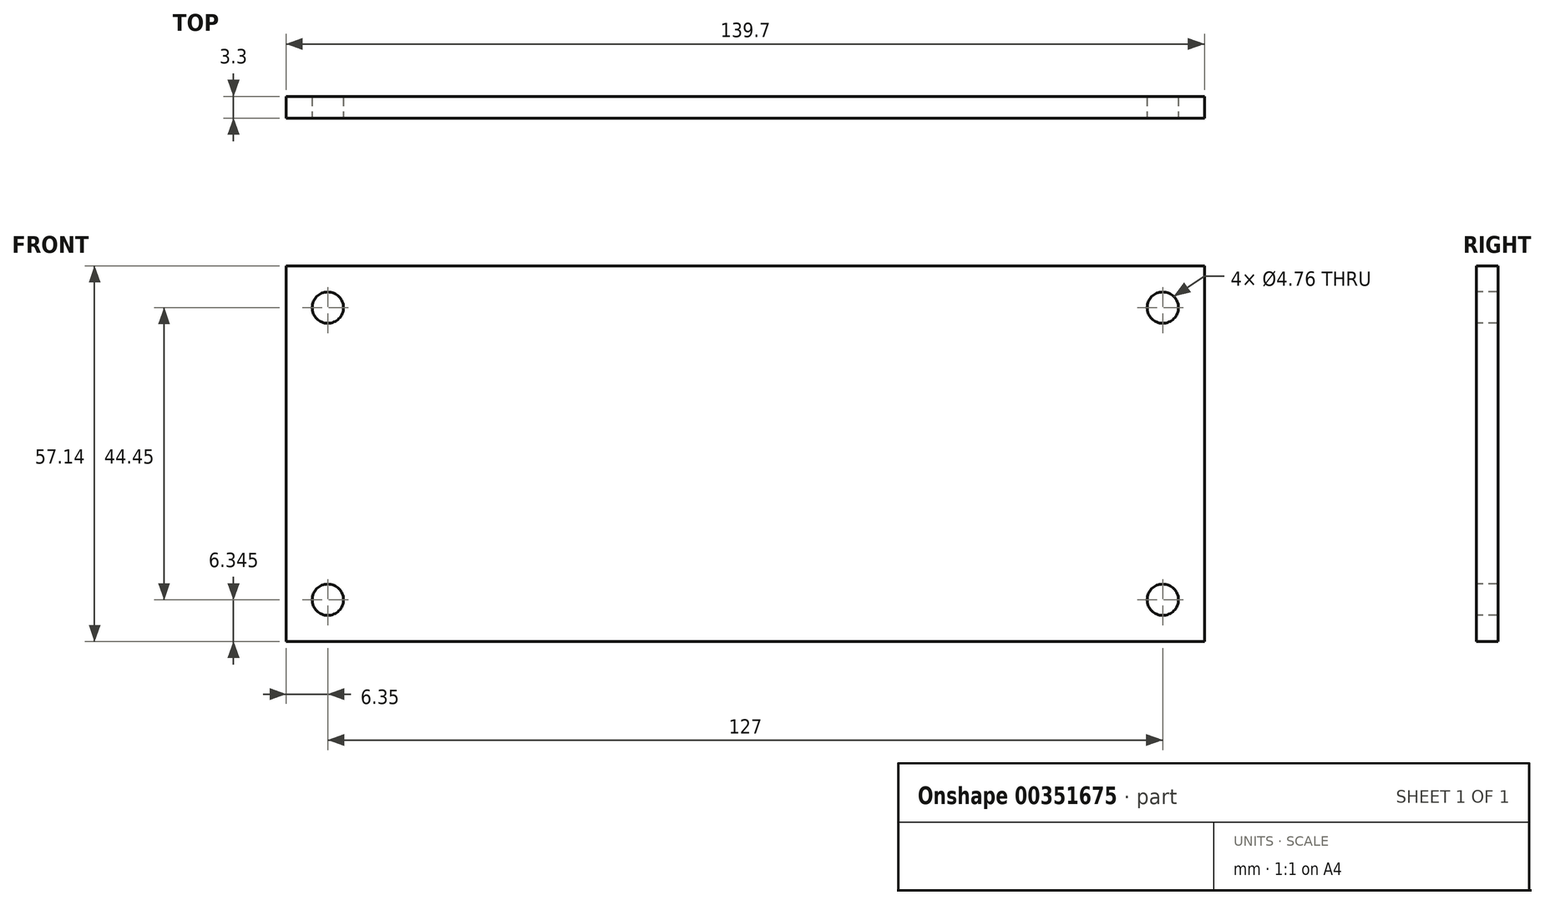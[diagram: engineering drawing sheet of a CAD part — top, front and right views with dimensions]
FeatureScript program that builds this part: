
annotation { "Feature Type Name" : "Feature", "Feature Type Description" : "" }
export const myFeature = defineFeature(function(context is Context, id is Id, definition is map)
    precondition{}
    {
        {
            var Q0;
            Q0=qCreatedBy(makeId("Front.planeOp"),FACE);
            var sketch = newSketch(context, id + "F0", { "sketchPlane" : qUnion([Q0])});
            skLineSegment(sketch, "E0.bottom", {"start": v(-69.85, 28.58) * mm, "end": v(69.85, 28.58) * mm});
            skLineSegment(sketch, "E0.top", {"start": v(-69.85, -28.58) * mm, "end": v(69.85, -28.58) * mm});
            skLineSegment(sketch, "E0.left", {"start": v(-69.85, 28.58) * mm, "end": v(-69.85, -28.57) * mm});
            skLineSegment(sketch, "E0.right", {"start": v(69.85, 28.58) * mm, "end": v(69.85, -28.57) * mm});
            skPoint(sketch, "E0.middle", {"position": v(0, 0) * mm});
            skSolve(sketch);
        }
        {
            var Q0;
            Q0 = qSketchRegion(id + "F0", true);
            extrude(context, id + "F1", {"entities" : qUnion([Q0]), "depth" : 3.3 * mm});
        }
        {
            var Q0;
            Q0=makeQuery(id+"F1.opExtrude","CAP_FACE",FACE,{"disambiguationData":[OSD([sQuery(id+"F0.wireOp",EDGE,"E0.bottom"),sQuery(id+"F0.wireOp",EDGE,"E0.top"),sQuery(id+"F0.wireOp",EDGE,"E0.left"),sQuery(id+"F0.wireOp",EDGE,"E0.right")])],"isStart":false});
            var sketch = newSketch(context, id + "F2", { "sketchPlane" : qUnion([Q0])});
            skCircle(sketch, "E1", {"center": v(-63.5, 22.23) * mm, "radius": 2.38 * mm});
            skSolve(sketch);
        }
        {
            var Q0;
            Q0=makeQuery(id+"F2.imprint","IMPRINT",FACE,{"disambiguationData":[TD([[makeQuery(id+"F2.imprint","IMPRINT",EDGE,{"derivedFrom":sQuery(id+"F2.wireOp",EDGE,"E1")}),-1.0]])]});
            var sketch = newSketch(context, id + "F3", { "sketchPlane" : qUnion([Q0])});
            skCircle(sketch, "E2", {"center": v(-63.5, -22.23) * mm, "radius": 2.38 * mm});
            skSolve(sketch);
        }
        {
            var Q0;
            Q0 = qSketchRegion(id + "F2", true);
            extrude(context, id + "F4", {"entities" : qUnion([Q0]), "operationType" : NewBodyOperationType.REMOVE, "oppositeDirection" : true, "depth" : 3.3 * mm});
        }
        {
            var Q0;
            Q0 = qSketchRegion(id + "F3", true);
            extrude(context, id + "F5", {"entities" : qUnion([Q0]), "operationType" : NewBodyOperationType.REMOVE, "oppositeDirection" : true, "depth" : 3.3 * mm});
        }
        {
            var Q0;
            Q0=makeQuery(id+"F1.opExtrude","CAP_FACE",FACE,{"disambiguationData":[OSD([sQuery(id+"F0.wireOp",EDGE,"E0.bottom"),sQuery(id+"F0.wireOp",EDGE,"E0.top"),sQuery(id+"F0.wireOp",EDGE,"E0.left"),sQuery(id+"F0.wireOp",EDGE,"E0.right")])],"isStart":false});
            var sketch = newSketch(context, id + "F6", { "sketchPlane" : qUnion([Q0])});
            skCircle(sketch, "E3", {"center": v(63.5, 22.23) * mm, "radius": 2.38 * mm});
            skSolve(sketch);
        }
        {
            var Q0;
            Q0 = qSketchRegion(id + "F6", true);
            extrude(context, id + "F7", {"entities" : qUnion([Q0]), "operationType" : NewBodyOperationType.REMOVE, "oppositeDirection" : true, "depth" : 3.3 * mm});
        }
        {
            var Q0;
            Q0=makeQuery(id+"F1.opExtrude","CAP_FACE",FACE,{"disambiguationData":[OSD([sQuery(id+"F0.wireOp",EDGE,"E0.bottom"),sQuery(id+"F0.wireOp",EDGE,"E0.top"),sQuery(id+"F0.wireOp",EDGE,"E0.left"),sQuery(id+"F0.wireOp",EDGE,"E0.right")])],"isStart":false});
            var sketch = newSketch(context, id + "F8", { "sketchPlane" : qUnion([Q0])});
            skCircle(sketch, "E4", {"center": v(63.5, -22.23) * mm, "radius": 2.38 * mm});
            skSolve(sketch);
        }
        {
            var Q0;
            Q0 = qSketchRegion(id + "F8", true);
            extrude(context, id + "F9", {"entities" : qUnion([Q0]), "operationType" : NewBodyOperationType.REMOVE, "oppositeDirection" : true, "depth" : 3.3 * mm});
        }
    });
